# Revit family: CMB-M108V-JA1(-TR)
name_source: partatom
category: 機械設備
revit_build: Autodesk Revit 2016 (Build: 20150220_1215(x64)
units: mm (PartAtom-declared; Revit-internal decimal feet)

## family parameters
OmniClass タイトル = Climate Control (HVAC)
OmniClass 番号 = 23.75.00.00
パーツ タイプ = 標準
ホスト = 天井
ロード時にボイドで切り取り = いいえ
丸型コネクタ寸法 = 半径を使用
共有 = いいえ
常に垂直 = はい
部屋の計算ポイント = いいえ

## types (6) — shared parameters
Connectable Outdoor/Heat source Unit Capacity = P200 to P900/M200 to M300
Connection pipe of indoor unit (Gas Pipe)_radius (O.D.) = Indoor unit Model 50 or smaller 6.35 Brazed
bigger than 50 7.94 Brazed
(9.525, 11.1 with optional joint pipe used.)
Connection pipe of indoor unit (Liquid Pipe)_radius (O.D.) = Indoor unit Model 50 or smaller 3.175 Brazed
bigger than 50 4.76 Brazed
Connection pipe of other BC controller to M201 to M300 (High pressure Pipe)_radius = 7.94  [stored 0.0260499 ft]
Connection pipe of other BC controller to M201 to M300 (Liquid Pipe)_radius = 4.76
Connection pipe of other BC controller to M201 to M300 (Low pressure Pipe)_radius = 11.1  [stored 0.0364173 ft]
Connection pipe of other BC controller to M301 to M350 (High pressure Pipe)_radius = 7.94  [stored 0.0260499 ft]
Connection pipe of other BC controller to M301 to M350 (Liquid Pipe)_radius = 6.35  [stored 0.0208333 ft]
Connection pipe of other BC controller to M301 to M350 (Low pressure Pipe)_radius = 14.29  [stored 0.0468832 ft]
Connection pipe of other BC controller to M351 to M400 (High pressure Pipe)_radius = 9.53
Connection pipe of other BC controller to M351 to M400 (Liquid Pipe)_radius = 6.35  [stored 0.0208333 ft]
Connection pipe of other BC controller to M351 to M400 (Low pressure Pipe)_radius = 14.29  [stored 0.0468832 ft]
Connection pipe of other BC controller to M401 to M450 (High pressure Pipe)_radius = 9.53
Connection pipe of other BC controller to M401 to M450 (Liquid Pipe)_radius = 7.94  [stored 0.0260499 ft]
Connection pipe of other BC controller to M401 to M450 (Low pressure Pipe)_radius = 14.29  [stored 0.0468832 ft]
Connection pipe of other BC controller to P1001 or above (Liquid Pipe)_radius = 9.53
Connection pipe of other BC controller to P1001 or above (Low pressure Pipe)_radius = 20.64  [stored 0.0677165 ft]
Connection pipe of other BC controller to P1001 ot above (High pressure Pipe)_radius = 17.47
Connection pipe of other BC controller to P200/M200 (High pressure Pipe)_radius = 7.94  [stored 0.0260499 ft]
Connection pipe of other BC controller to P200/M200 (Liquid Pipe)_radius = 4.76
Connection pipe of other BC controller to P200/M200 (Low pressure Pipe)_radius = 9.53
Connection pipe of other BC controller to P201 to P300 (High pressure Pipe)_radius = 9.53
Connection pipe of other BC controller to P201 to P300 (Liquid Pipe)_radius = 4.76
Connection pipe of other BC controller to P201 to P300 (Low pressure Pipe)_radius = 11.1  [stored 0.0364173 ft]
Connection pipe of other BC controller to P301 to P350 (High pressure Pipe)_radius = 9.53
Connection pipe of other BC controller to P301 to P350 (Liquid Pipe)_radius = 6.35  [stored 0.0208333 ft]
Connection pipe of other BC controller to P301 to P350 (Low pressure Pipe)_radius = 14.29  [stored 0.0468832 ft]
Connection pipe of other BC controller to P351 to P400 (High pressure Pipe)_radius = 11.1  [stored 0.0364173 ft]
Connection pipe of other BC controller to P351 to P400 (Liquid Pipe)_radius = 6.35  [stored 0.0208333 ft]
Connection pipe of other BC controller to P351 to P400 (Low pressure Pipe)_radius = 14.29  [stored 0.0468832 ft]
Connection pipe of other BC controller to P401 to P600 (High pressure Pipe)_radius = 11.1  [stored 0.0364173 ft]
Connection pipe of other BC controller to P401 to P600 (Liquid Pipe)_radius = 7.94  [stored 0.0260499 ft]
Connection pipe of other BC controller to P401 to P600 (Low pressure Pipe)_radius = 14.29  [stored 0.0468832 ft]
Connection pipe of other BC controller to P601 to P650 (High pressure Pipe)_radius = 14.29  [stored 0.0468832 ft]
Connection pipe of other BC controller to P601 to P650 (Liquid Pipe)_radius = 7.94  [stored 0.0260499 ft]
Connection pipe of other BC controller to P601 to P650 (Low pressure Pipe)_radius = 14.29  [stored 0.0468832 ft]
Connection pipe of other BC controller to P651 to P800 (High pressure Pipe)_radius = 14.29  [stored 0.0468832 ft]
Connection pipe of other BC controller to P651 to P800 (Liquid Pipe)_radius = 9.53
Connection pipe of other BC controller to P651 to P800 (Low pressure Pipe)_radius = 17.47
Connection pipe of other BC controller to P801 to P1000 (High pressure Pipe)_radius = 14.29  [stored 0.0468832 ft]
Connection pipe of other BC controller to P801 to P1000 (Liquid Pipe)_radius = 9.53
Connection pipe of other BC controller to P801 to P1000 (Low pressure Pipe)_radius = 20.64  [stored 0.0677165 ft]
Connection pipe of outdoor/heat source unit to M250/M300 (High pressure)_radius = 7.94  [stored 0.0260499 ft]
Connection pipe of outdoor/heat source unit to M250/M300 (Low pressure)_radius = 11.1  [stored 0.0364173 ft]
Connection pipe of outdoor/heat source unit to P200/M200 (High pressure)_radius = 7.94  [stored 0.0260499 ft]
Connection pipe of outdoor/heat source unit to P200/M200 (Low pressure)_radius = 9.53
Connection pipe of outdoor/heat source unit to P250/P300 (High pressure)_radius = 9.53
Connection pipe of outdoor/heat source unit to P250/P300 (Low pressure)_radius = 11.1  [stored 0.0364173 ft]
Connection pipe of outdoor/heat source unit to P350 (High pressure) radius = 9.525 or 11.1
Connection pipe of outdoor/heat source unit to P350 (Low pressure)_radius = 14.29  [stored 0.0468832 ft]
Connection pipe of outdoor/heat source unit to P400 to P500 (High pressure)_radius = 11.1  [stored 0.0364173 ft]
Connection pipe of outdoor/heat source unit to P400 to P500 (Low pressure)_radius = 14.29  [stored 0.0468832 ft]
Connection pipe of outdoor/heat source unit to P550 (High pressure) radius = 11.1 or 14.29
Connection pipe of outdoor/heat source unit to P550 (Low pressure)_radius = 14.29  [stored 0.0468832 ft]
Connection pipe of outdoor/heat source unit to P600 (High pressure) radius = 11.1 or 14.29
Connection pipe of outdoor/heat source unit to P600 (Low pressure) radius = 14.29 or 17.465
Connection pipe of outdoor/heat source unit to P650 (High pressure)_radius = 14.29  [stored 0.0468832 ft]
Connection pipe of outdoor/heat source unit to P650 (Low pressure)_radius = 14.29  [stored 0.0468832 ft]
Connection pipe of outdoor/heat source unit to P700 to P800 (High pressure)_radius = 14.29  [stored 0.0468832 ft]
Connection pipe of outdoor/heat source unit to P700 to P800 (Low pressure)_radius = 17.47
Connection pipe of outdoor/heat source unit to P850 to P900 (High pressure)_radius = 14.29  [stored 0.0468832 ft]
Connection pipe of outdoor/heat source unit to P850 to P900 (Low pressure)_radius = 20.64  [stored 0.0677165 ft]
Depth = 622  [stored 2.04068 ft]
Drain pipe_radius = 16  [stored 0.0524934 ft]
External Finish = Galvanized steel plate
(Lower part drain pan: Pre-coated galvanized sheets + powder coating)
Height = 252  [stored 0.826772 ft]
Indoor unit capacity connectable to 1 branch = Model P/M80 or smaller
(Use optional joint pipe combining 2 branches when the total unit capacity exceeds P/M81.)
Number of branch = 8
Phase = 1
Sound Power Level (Defrost) (dB(A)) = 74
Sound Power Level (Rated operation) (dB(A)) = 68
Sound Pressure Level (Defrost) (dB(A)) = 56
Sound Pressure Level (Rated operation) (dB(A)) = 50
Space View = はい
Subcategory = HVAC
URL = http://www.mitsubishielectric.com
Unit Weight (kg) = 48
Width = 911  [stored 2.98885 ft]
モデル = CMB-M108V-JA1(-TR)
製造元 = Mitsubishi Electric Corporation
説明 = BC controller
zero-valued in all types: Equip_No., SerialNumber, TagNumber

## per-type parameters (varying)
| type | Cooling Current (A) | Cooling Power Input (kW) | Heating Current (A) | Heating Power Input (kW) | Hertz | Voltage |
| CMB-M108V-JA1(-TR)_220V_50Hz | 0.58 | 0.127 | 0.28 | 0.06 | 50 Hz | 220 V |
| CMB-M108V-JA1(-TR)_220V_60Hz | 0.47 | 0.102 | 0.22 | 0.048 | 60 Hz | 220 V |
| CMB-M108V-JA1(-TR)_230V_50Hz | 0.63 | 0.144 | 0.3 | 0.068 | 50 Hz | 230 V |
| CMB-M108V-JA1(-TR)_230V_60Hz | 0.5 | 0.115 | 0.24 | 0.054 | 60 Hz | 230 V |
| CMB-M108V-JA1(-TR)_240V_50Hz | 0.68 | 0.161 | 0.32 | 0.076 | 50 Hz | 240 V |
| CMB-M108V-JA1(-TR)_240V_60Hz | 0.53 | 0.127 | 0.25 | 0.06 | 60 Hz | 240 V |

note: [stored X ft] marks values corroborated as IEEE doubles in the binary element streams (Revit-internal decimal feet)

## geometry (parser evidence)
native form markers: Blend x80, Sweep x1
no freeform markers — native parametric forms only
